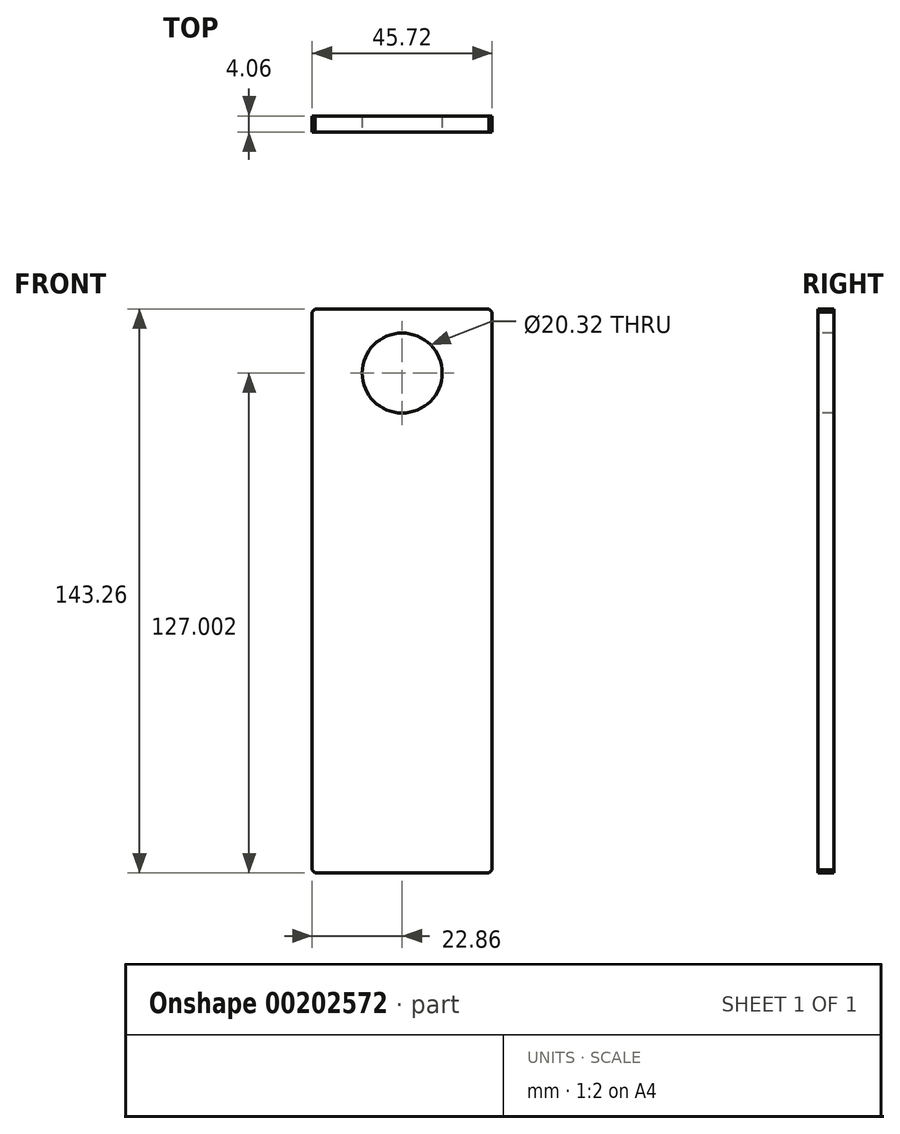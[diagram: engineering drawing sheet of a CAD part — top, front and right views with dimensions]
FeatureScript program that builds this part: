
annotation { "Feature Type Name" : "Feature", "Feature Type Description" : "" }
export const myFeature = defineFeature(function(context is Context, id is Id, definition is map)
    precondition{}
    {
        {
            var Q0;
            Q0=qCreatedBy(makeId("Front.planeOp"),FACE);
            var sketch = newSketch(context, id + "F0", { "sketchPlane" : qUnion([Q0])});
            skLineSegment(sketch, "E0.bottom", {"start": v(-22.86, 71.63) * mm, "end": v(22.86, 71.63) * mm});
            skLineSegment(sketch, "E0.top", {"start": v(-22.86, -71.63) * mm, "end": v(22.86, -71.63) * mm});
            skLineSegment(sketch, "E0.left", {"start": v(-22.86, 71.63) * mm, "end": v(-22.86, -71.63) * mm});
            skLineSegment(sketch, "E0.right", {"start": v(22.86, 71.63) * mm, "end": v(22.86, -71.63) * mm});
            skSolve(sketch);
        }
        {
            var Q0;
            Q0=makeQuery(id+"F0.imprint","IMPRINT",FACE,{"disambiguationData":[TD([[makeQuery(id+"F0.imprint","IMPRINT",EDGE,{"derivedFrom":sQuery(id+"F0.wireOp",EDGE,"E0.bottom")}),-1.0]])]});
            extrude(context, id + "F1", {"entities" : qUnion([Q0]), "depth" : 4.06 * mm});
        }
        {
            var Q0;
            Q0=makeQuery(id+"F1.opExtrude","SWEPT_EDGE",EDGE,{"disambiguationData":[OSD([sQuery(id+"F0.wireOp",EDGE,"E0.bottom"),sQuery(id+"F0.wireOp",EDGE,"E0.right")])]});
            var Q1;
            Q1=makeQuery(id+"F1.opExtrude","SWEPT_EDGE",EDGE,{"disambiguationData":[OSD([sQuery(id+"F0.wireOp",EDGE,"E0.bottom"),sQuery(id+"F0.wireOp",EDGE,"E0.left")])]});
            var Q2;
            Q2=makeQuery(id+"F1.opExtrude","SWEPT_EDGE",EDGE,{"disambiguationData":[OSD([sQuery(id+"F0.wireOp",EDGE,"E0.top"),sQuery(id+"F0.wireOp",EDGE,"E0.left")])]});
            var Q3;
            Q3=makeQuery(id+"F1.opExtrude","SWEPT_EDGE",EDGE,{"disambiguationData":[OSD([sQuery(id+"F0.wireOp",EDGE,"E0.top"),sQuery(id+"F0.wireOp",EDGE,"E0.right")])]});
            chamfer(context, id + "F2", {"entities" : qUnion([Q0, Q1, Q2, Q3]), "chamferType" : ChamferType.OFFSET_ANGLE, "width" : 0.76 * mm, "oppositeDirection" : false, "angle" : 45 * degree, "tangentPropagation" : true});
        }
        {
            var Q0;
            Q0=makeQuery(id+"F1.opExtrude","CAP_FACE",FACE,{"disambiguationData":[OSD([sQuery(id+"F0.wireOp",EDGE,"E0.bottom"),sQuery(id+"F0.wireOp",EDGE,"E0.top"),sQuery(id+"F0.wireOp",EDGE,"E0.left"),sQuery(id+"F0.wireOp",EDGE,"E0.right")])],"isStart":false});
            var sketch = newSketch(context, id + "F3", { "sketchPlane" : qUnion([Q0])});
            skCircle(sketch, "E1", {"center": v(0, 55.37) * mm, "radius": 10.16 * mm});
            skSolve(sketch);
        }
        {
            var Q0;
            Q0=sQuery(id+"F3.wireOp",VERTEX,"E1.center");
            var Q1;
            Q1=makeQuery(id+"F1.opExtrude","SWEPT_BODY",BODY,{"disambiguationData":[OSD([sQuery(id+"F0.wireOp",EDGE,"E0.bottom"),sQuery(id+"F0.wireOp",EDGE,"E0.top"),sQuery(id+"F0.wireOp",EDGE,"E0.left"),sQuery(id+"F0.wireOp",EDGE,"E0.right")])]});
            hole(context, id + "F4", {"style" : HoleStyle.SIMPLE, "endStyle" : HoleEndStyle.THROUGH, "holeDiameter" : 20.32 * mm, "locations" : qUnion([Q0]), "scope" : qUnion([Q1]), "isTappedThrough" : true});
        }
    });
